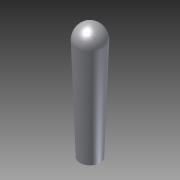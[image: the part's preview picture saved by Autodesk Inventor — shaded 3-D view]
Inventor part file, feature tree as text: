
AUTODESK INVENTOR PART (.ipt)
format: ipt  version: 2011 SP1 (Build 150282100, 282)  size: 91,648 bytes
history: native  units: in
note: dims shown in document units (in); Inventor stores cm internally (conversion verified against a paired STEP export)
features: other x7, revolve x1, sketch x1
ambient origin geometry x8: Origin, YZ Plane, XZ Plane, XY Plane, X Axis, Y Axis, Z Axis, Center Point
bodies: Solid1 (feature_tree)
feature tree (9):
  revolve  "Revolution1"  [1 undecoded]
  other  "to_body1_XY"
  other  "to_body1_YZ"
  other  "to_body1_ZX"
  other  "to_body1_X"
  other  "to_body1_Y"
  other  "to_body1_Z"
  other  "to_body1_Center"
  sketch  "Sketch_1"  dims[d0=360.0deg]
note: 1 required parameter value undecoded (feature->parameter linkage not recoverable at this tier; creation-order binding heuristic only, values carry confidence <= 0.55)
